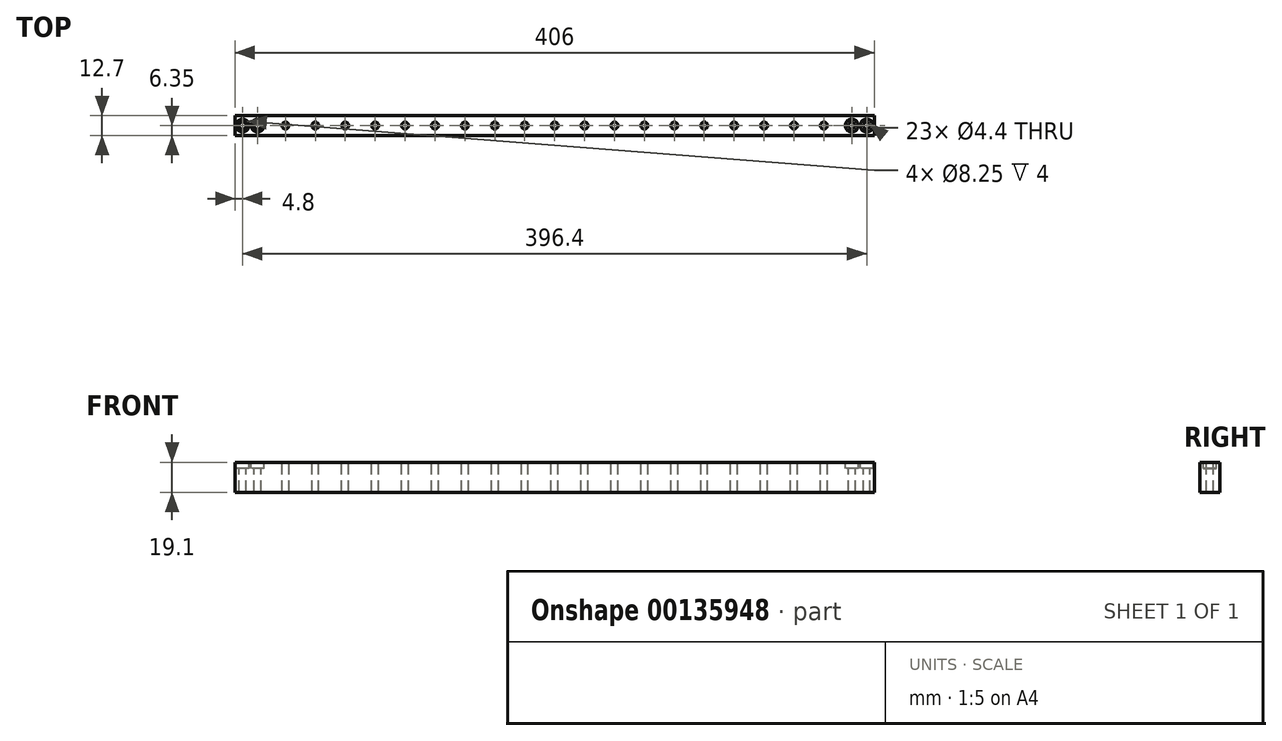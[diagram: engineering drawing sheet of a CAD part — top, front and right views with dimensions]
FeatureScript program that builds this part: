
annotation { "Feature Type Name" : "Feature", "Feature Type Description" : "" }
export const myFeature = defineFeature(function(context is Context, id is Id, definition is map)
    precondition{}
    {
        {
            var Q0;
            Q0=qCreatedBy(makeId("Top.planeOp"),FACE);
            var sketch = newSketch(context, id + "F0", { "sketchPlane" : qUnion([Q0])});
            skLineSegment(sketch, "E0.bottom", {"start": v(203, -6.35) * mm, "end": v(-203, -6.35) * mm});
            skLineSegment(sketch, "E0.top", {"start": v(203, 6.35) * mm, "end": v(-203, 6.35) * mm});
            skLineSegment(sketch, "E0.left", {"start": v(203, -6.35) * mm, "end": v(203, 6.35) * mm});
            skLineSegment(sketch, "E0.right", {"start": v(-203, -6.35) * mm, "end": v(-203, 6.35) * mm});
            skPoint(sketch, "E0.middle", {"position": v(0, 0) * mm});
            skSolve(sketch);
        }
        {
            var Q0;
            Q0 = qSketchRegion(id + "F0", true);
            extrude(context, id + "F1", {"entities" : qUnion([Q0]), "endBound" : BoundingType.SYMMETRIC, "depth" : 19.1 * mm});
        }
        {
            var Q0;
            Q0=makeQuery(id+"F1.opExtrude","CAP_FACE",FACE,{"disambiguationData":[OSD([sQuery(id+"F0.wireOp",EDGE,"E0.bottom"),sQuery(id+"F0.wireOp",EDGE,"E0.top"),sQuery(id+"F0.wireOp",EDGE,"E0.left"),sQuery(id+"F0.wireOp",EDGE,"E0.right")])],"isStart":false});
            var sketch = newSketch(context, id + "F2", { "sketchPlane" : qUnion([Q0])});
            skCircle(sketch, "E1", {"center": v(-198.2, 0) * mm, "radius": 2 * mm});
            skCircle(sketch, "E2", {"center": v(-188.7, 0) * mm, "radius": 2 * mm});
            skCircle(sketch, "E3.MirrorC", {"center": v(188.7, 0) * mm, "radius": 2 * mm});
            skCircle(sketch, "E4.MirrorC", {"center": v(198.2, 0) * mm, "radius": 2 * mm});
            skSolve(sketch);
        }
        {
            var Q0;
            Q0=sQuery(id+"F2.wireOp",VERTEX,"E1.center");
            var Q1;
            Q1=sQuery(id+"F2.wireOp",VERTEX,"E2.center");
            var Q2;
            Q2=sQuery(id+"F2.wireOp",VERTEX,"E3.MirrorC.center");
            var Q3;
            Q3=sQuery(id+"F2.wireOp",VERTEX,"E4.MirrorC.center");
            var Q4;
            Q4=makeQuery(id+"F1.opExtrude","SWEPT_BODY",BODY,{"disambiguationData":[OSD([sQuery(id+"F0.wireOp",EDGE,"E0.bottom"),sQuery(id+"F0.wireOp",EDGE,"E0.top"),sQuery(id+"F0.wireOp",EDGE,"E0.left"),sQuery(id+"F0.wireOp",EDGE,"E0.right")])]});
            hole(context, id + "F3", {"style" : HoleStyle.C_BORE, "endStyle" : HoleEndStyle.BLIND, "standardTappedOrClearance" : lookupTablePath({ "standard" : "ISO", "fit" : "Normal", "size" : "M4", "type" : "Clearance" }), "standardBlindInLast" : lookupTablePath({ "fit" : "Standard", "standard" : "ISO", "size" : "M4", "type" : "Clearance" }), "holeDiameter" : 4.4 * mm, "cBoreDiameter" : 8.25 * mm, "cBoreDepth" : 4 * mm, "holeDepth" : 20 * mm, "locations" : qUnion([Q0, Q1, Q2, Q3]), "scope" : qUnion([Q4])});
        }
        {
            var Q0;
            Q0=makeQuery(id+"F1.opExtrude","CAP_FACE",FACE,{"disambiguationData":[OSD([sQuery(id+"F0.wireOp",EDGE,"E0.bottom"),sQuery(id+"F0.wireOp",EDGE,"E0.top"),sQuery(id+"F0.wireOp",EDGE,"E0.left"),sQuery(id+"F0.wireOp",EDGE,"E0.right")])],"isStart":false});
            var sketch = newSketch(context, id + "F4", { "sketchPlane" : qUnion([Q0])});
            skCircle(sketch, "E5", {"center": v(-171, 0) * mm, "radius": 2.19 * mm});
            skCircle(sketch, "E6.1.0.0", {"center": v(-152, 0) * mm, "radius": 2.19 * mm});
            skCircle(sketch, "E6.2.0.0", {"center": v(-133, 0) * mm, "radius": 2.19 * mm});
            skCircle(sketch, "E6.3.0.0", {"center": v(-114, 0) * mm, "radius": 2.19 * mm});
            skCircle(sketch, "E6.4.0.0", {"center": v(-95, 0) * mm, "radius": 2.19 * mm});
            skCircle(sketch, "E6.5.0.0", {"center": v(-76, 0) * mm, "radius": 2.19 * mm});
            skCircle(sketch, "E6.6.0.0", {"center": v(-57, 0) * mm, "radius": 2.19 * mm});
            skCircle(sketch, "E6.7.0.0", {"center": v(-38, 0) * mm, "radius": 2.19 * mm});
            skCircle(sketch, "E6.8.0.0", {"center": v(-19, 0) * mm, "radius": 2.19 * mm});
            skCircle(sketch, "E6.9.0.0", {"center": v(0, 0) * mm, "radius": 2.19 * mm});
            skCircle(sketch, "E6.10.0.0", {"center": v(19, 0) * mm, "radius": 2.19 * mm});
            skCircle(sketch, "E6.11.0.0", {"center": v(38, 0) * mm, "radius": 2.19 * mm});
            skCircle(sketch, "E6.12.0.0", {"center": v(57, 0) * mm, "radius": 2.19 * mm});
            skCircle(sketch, "E6.13.0.0", {"center": v(76, 0) * mm, "radius": 2.19 * mm});
            skCircle(sketch, "E6.14.0.0", {"center": v(95, 0) * mm, "radius": 2.19 * mm});
            skCircle(sketch, "E6.15.0.0", {"center": v(114, 0) * mm, "radius": 2.19 * mm});
            skCircle(sketch, "E6.16.0.0", {"center": v(133, 0) * mm, "radius": 2.19 * mm});
            skCircle(sketch, "E6.17.0.0", {"center": v(152, 0) * mm, "radius": 2.19 * mm});
            skCircle(sketch, "E6.18.0.0", {"center": v(171, 0) * mm, "radius": 2.19 * mm});
            skLineSegment(sketch, "E6.direction1", {"start": v(-171, 0) * mm, "end": v(-152, 0) * mm, "construction": true});
            skSolve(sketch);
        }
        {
            var Q0;
            Q0=sQuery(id+"F4.wireOp",VERTEX,"E5.center");
            var Q1;
            Q1=sQuery(id+"F4.wireOp",VERTEX,"E6.1.0.0.center");
            var Q2;
            Q2=sQuery(id+"F4.wireOp",VERTEX,"E6.2.0.0.center");
            var Q3;
            Q3=sQuery(id+"F4.wireOp",VERTEX,"E6.3.0.0.center");
            var Q4;
            Q4=sQuery(id+"F4.wireOp",VERTEX,"E6.4.0.0.center");
            var Q5;
            Q5=sQuery(id+"F4.wireOp",VERTEX,"E6.6.0.0.center");
            var Q6;
            Q6=sQuery(id+"F4.wireOp",VERTEX,"E6.7.0.0.center");
            var Q7;
            Q7=sQuery(id+"F4.wireOp",VERTEX,"E6.5.0.0.center");
            var Q8;
            Q8=sQuery(id+"F4.wireOp",VERTEX,"E6.8.0.0.center");
            var Q9;
            Q9=sQuery(id+"F4.wireOp",VERTEX,"E6.9.0.0.center");
            var Q10;
            Q10=sQuery(id+"F4.wireOp",VERTEX,"E6.10.0.0.center");
            var Q11;
            Q11=sQuery(id+"F4.wireOp",VERTEX,"E6.11.0.0.center");
            var Q12;
            Q12=sQuery(id+"F4.wireOp",VERTEX,"E6.12.0.0.center");
            var Q13;
            Q13=sQuery(id+"F4.wireOp",VERTEX,"E6.13.0.0.center");
            var Q14;
            Q14=sQuery(id+"F4.wireOp",VERTEX,"E6.14.0.0.center");
            var Q15;
            Q15=sQuery(id+"F4.wireOp",VERTEX,"E6.15.0.0.center");
            var Q16;
            Q16=sQuery(id+"F4.wireOp",VERTEX,"E6.16.0.0.center");
            var Q17;
            Q17=sQuery(id+"F4.wireOp",VERTEX,"E6.17.0.0.center");
            var Q18;
            Q18=sQuery(id+"F4.wireOp",VERTEX,"E6.18.0.0.center");
            var Q19;
            Q19=sQuery(id+"F4.wireOp",VERTEX,"E6.16.0.0.center");
            var Q20;
            Q20=makeQuery(id+"F1.opExtrude","SWEPT_BODY",BODY,{"disambiguationData":[OSD([sQuery(id+"F0.wireOp",EDGE,"E0.bottom"),sQuery(id+"F0.wireOp",EDGE,"E0.top"),sQuery(id+"F0.wireOp",EDGE,"E0.left"),sQuery(id+"F0.wireOp",EDGE,"E0.right")])]});
            hole(context, id + "F5", {"style" : HoleStyle.SIMPLE, "endStyle" : HoleEndStyle.THROUGH, "standardTappedOrClearance" : lookupTablePath({ "standard" : "ISO", "fit" : "Normal", "size" : "M4", "type" : "Clearance" }), "standardBlindInLast" : lookupTablePath({ "fit" : "Standard", "standard" : "ISO", "size" : "M4", "type" : "Clearance" }), "holeDiameter" : 4.4 * mm, "locations" : qUnion([Q0, Q1, Q2, Q3, Q4, Q5, Q6, Q7, Q8, Q9, Q10, Q11, Q12, Q13, Q14, Q15, Q16, Q17, Q18, Q19]), "scope" : qUnion([Q20]), "isTappedThrough" : true});
        }
    });
